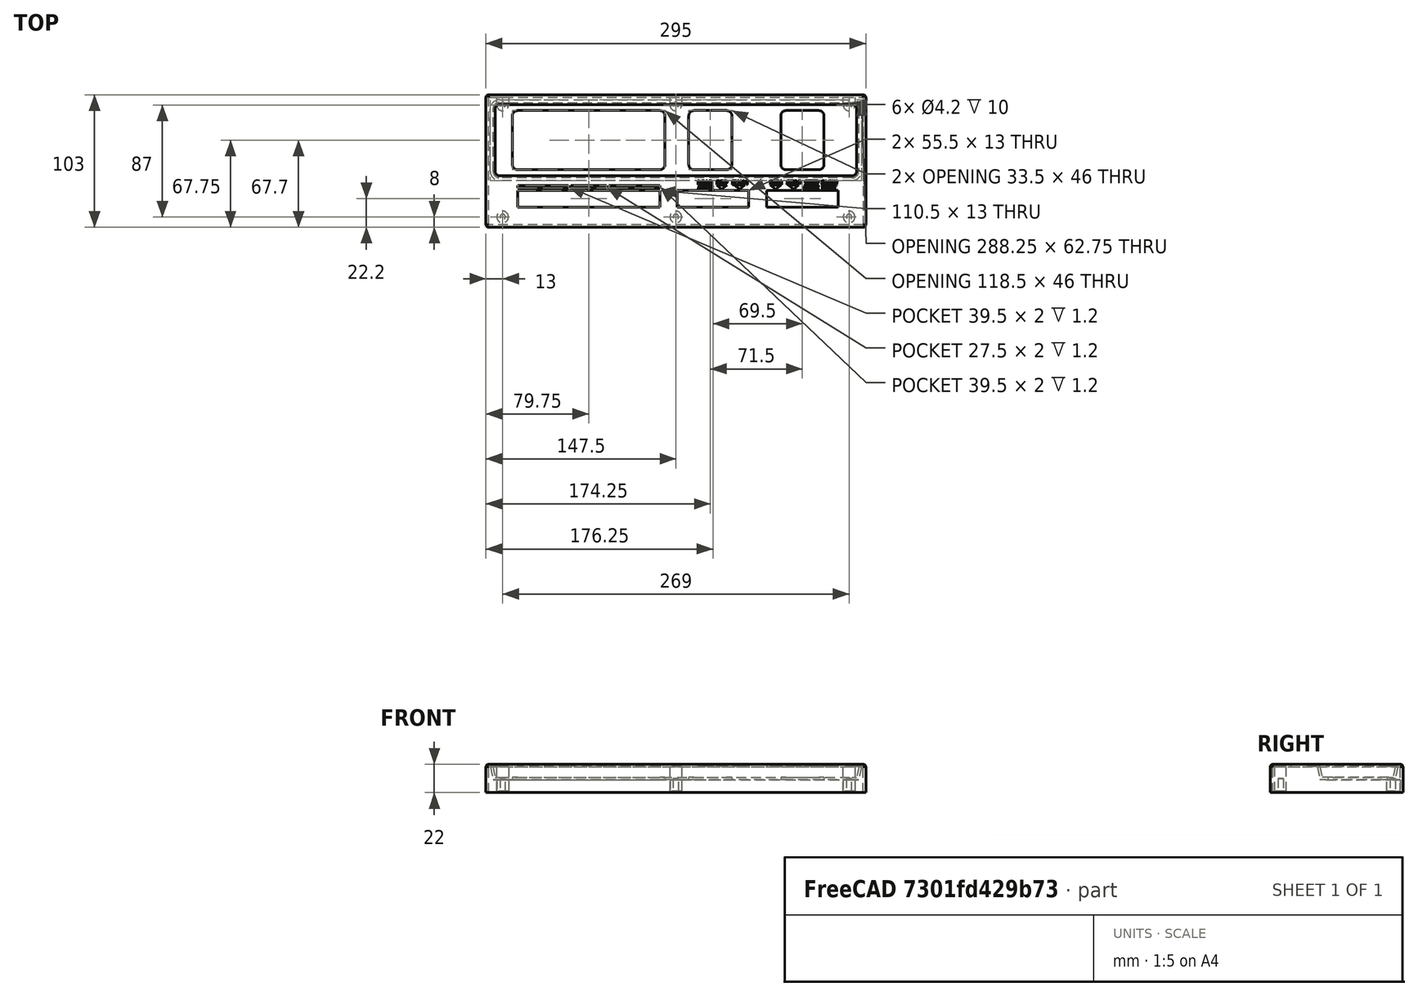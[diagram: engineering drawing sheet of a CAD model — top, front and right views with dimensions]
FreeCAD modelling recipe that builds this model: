
FCSTD DOCUMENT  (FreeCAD 0.21R33771 (Git))
Label: front panel
License: All rights reserved
LicenseURL: http://en.wikipedia.org/wiki/All_rights_reserved
objects: PartDesign::Pocket×14, Part::Part2DObjectPython×13, Sketcher::SketchObject×7, PartDesign::LinearPattern×4, PartDesign::Pad×3, TechDraw::DrawViewDimension×3, PartDesign::Draft×1, PartDesign::Thickness×1, PartDesign::MultiTransform×1, TechDraw::DrawSVGTemplate×1, PartDesign::Body×1, TechDraw::DrawProjGroupItem×1, TechDraw::DrawProjGroup×1, TechDraw::DrawPage×1
note: 69 computed .brp shape members not serialized (recipe doc carries the construction recipe); baked Part::Feature solids carry a one-line shape summary decoded from their .brp

FEATURE [Sketcher::SketchObject] Sketch
  FullyConstrained = true
  MapMode = 5
  Support = -> [XY_Plane]
  sketch-geometry (4):
    g0: LineSegment StartX=-145.5 StartY=49.5 StartZ=0 EndX=145.5 EndY=49.5 EndZ=0
    g1: LineSegment StartX=145.5 StartY=49.5 StartZ=0 EndX=145.5 EndY=-49.5 EndZ=0
    g2: LineSegment StartX=145.5 StartY=-49.5 StartZ=0 EndX=-145.5 EndY=-49.5 EndZ=0
    g3: LineSegment StartX=-145.5 StartY=-49.5 StartZ=0 EndX=-145.5 EndY=49.5 EndZ=0
  constraints (11):
    c: Coincident(g0,g1)
    c: Coincident(g1,g2)
    c: Coincident(g2,g3)
    c: Coincident(g3,g0)
    c: Horizontal(g0)
    c: Horizontal(g2)
    c: Vertical(g1)
    c: Vertical(g3)
    c: Symmetric(g1,g0,g-1)
    c: DistanceY(g3,g3) = 99
    c: DistanceX(g0,g0) = 291
FEATURE [PartDesign::Pad] Pad
  Direction = (0,0,1)
  Length = 20
  Length2 = 10
  Profile = -> Sketch
  ReferenceAxis = -> Sketch [N_Axis]
  Type = 0
FEATURE [Sketcher::SketchObject] Sketch001
  FullyConstrained = true
  MapMode = 5
  Placement = pos=(0,0,20) rot=(0,0,1;0rad)
  Support = -> [Pad]
  sketch-geometry (10):
    g0: ArcOfCircle CenterX=-137 CenterY=40.5 CenterZ=0 NormalX=0 NormalY=0 NormalZ=1 AngleXU=0 Radius=5 StartAngle=1.5708 EndAngle=3.14159
    g1: LineSegment StartX=-137 StartY=45.5 StartZ=0 EndX=137 EndY=45.5 EndZ=0
    g2: ArcOfCircle CenterX=137 CenterY=40.5 CenterZ=0 NormalX=0 NormalY=0 NormalZ=1 AngleXU=0 Radius=5 StartAngle=5e-16 EndAngle=1.5708
    g3: LineSegment StartX=142 StartY=40.5 StartZ=0 EndX=142 EndY=-8 EndZ=0
    g4: ArcOfCircle CenterX=137 CenterY=-8 CenterZ=0 NormalX=0 NormalY=0 NormalZ=1 AngleXU=0 Radius=5 StartAngle=4.71239 EndAngle=6.28319
    g5: LineSegment StartX=137 StartY=-13 StartZ=0 EndX=-137 EndY=-13 EndZ=0
    g6: ArcOfCircle CenterX=-137 CenterY=-8 CenterZ=0 NormalX=0 NormalY=0 NormalZ=1 AngleXU=0 Radius=5 StartAngle=3.14159 EndAngle=4.71239
    g7: LineSegment StartX=-142 StartY=-8 StartZ=0 EndX=-142 EndY=40.5 EndZ=0
    g8: GeomPoint X=-142 Y=45.5 Z=0
    g9: GeomPoint X=142 Y=-13 Z=0
  constraints (23):
    c: Tangent(g0,g1) = 1.5708
    c: Tangent(g1,g2) = 1.5708
    c: Tangent(g2,g3) = 1.5708
    c: Tangent(g3,g4) = 1.5708
    c: Tangent(g4,g5) = 1.5708
    c: Tangent(g5,g6) = 1.5708
    c: Tangent(g6,g7) = 1.5708
    c: Tangent(g7,g0) = 1.5708
    c: Horizontal(g1)
    c: Horizontal(g5)
    c: Vertical(g3)
    c: Vertical(g7)
    c: Equal(g2,g4)
    c: Equal(g4,g6)
    c: PointOnObject(g8,g1)
    c: PointOnObject(g8,g7)
    c: PointOnObject(g9,g3)
    c: PointOnObject(g9,g5)
    c: Diameter(g2) = 10
    c: DistanceX(g0,g2) = 284
    c: Symmetric(g0,g2,g-2)
    c: DistanceY(g-1,g0) = 45.5
    c: DistanceY(g5,g-1) = 13
FEATURE [PartDesign::Pocket] Pocket
  BaseFeature = -> Pad
  Direction = (0,0,-1)
  Length = 10
  Length2 = 5
  Profile = -> Sketch001
  ReferenceAxis = -> Sketch001 [N_Axis]
  Type = 0
FEATURE [PartDesign::Draft] Draft
  Angle = 12
  Base = -> Pocket [Face10]
  BaseFeature = -> Pocket
  NeutralPlane = -> Pocket [Face15]
  SupportTransform = false
FEATURE [PartDesign::Thickness] Thickness
  Base = -> Draft [Face4]
  BaseFeature = -> Draft
  Intersection = false
  Join = 0
  Mode = 0
  SupportTransform = false
  Value = 2
FEATURE [Sketcher::SketchObject] Sketch002
  FullyConstrained = true
  MapMode = 5
  Placement = pos=(0,0,22) rot=(0,0,1;0rad)
  Support = -> [Thickness]
  sketch-geometry (42):
    g0: LineSegment StartX=-123 StartY=-22.8 StartZ=0 EndX=-12.5 EndY=-22.8 EndZ=0
    g1: LineSegment StartX=-12.5 StartY=-22.8 StartZ=0 EndX=-12.5 EndY=-35.8 EndZ=0
    g2: LineSegment StartX=-12.5 StartY=-35.8 StartZ=0 EndX=-123 EndY=-35.8 EndZ=0
    g3: LineSegment StartX=-123 StartY=-35.8 StartZ=0 EndX=-123 EndY=-22.8 EndZ=0
    g4: LineSegment StartX=1 StartY=-22.8 StartZ=0 EndX=56.5 EndY=-22.8 EndZ=0
    g5: LineSegment StartX=56.5 StartY=-22.8 StartZ=0 EndX=56.5 EndY=-35.8 EndZ=0
    g6: LineSegment StartX=56.5 StartY=-35.8 StartZ=0 EndX=1 EndY=-35.8 EndZ=0
    g7: LineSegment StartX=1 StartY=-35.8 StartZ=0 EndX=1 EndY=-22.8 EndZ=0
    g8: LineSegment StartX=70.5 StartY=-22.8 StartZ=0 EndX=126 EndY=-22.8 EndZ=0
    g9: LineSegment StartX=126 StartY=-22.8 StartZ=0 EndX=126 EndY=-35.8 EndZ=0
    g10: LineSegment StartX=126 StartY=-35.8 StartZ=0 EndX=70.5 EndY=-35.8 EndZ=0
    g11: LineSegment StartX=70.5 StartY=-35.8 StartZ=0 EndX=70.5 EndY=-22.8 EndZ=0
    g12: ArcOfCircle CenterX=-123 CenterY=35.2 CenterZ=0 NormalX=0 NormalY=0 NormalZ=1 AngleXU=0 Radius=4 StartAngle=1.5708 EndAngle=3.14159
    g13: LineSegment StartX=-123 StartY=39.2 StartZ=0 EndX=-12.5 EndY=39.2 EndZ=0
    g14: ArcOfCircle CenterX=-12.5 CenterY=35.2 CenterZ=0 NormalX=0 NormalY=0 NormalZ=1 AngleXU=0 Radius=4 StartAngle=1e-15 EndAngle=1.5708
    g15: LineSegment StartX=-8.5 StartY=35.2 StartZ=0 EndX=-8.5 EndY=-2.8 EndZ=0
    g16: ArcOfCircle CenterX=-12.5 CenterY=-2.8 CenterZ=0 NormalX=0 NormalY=0 NormalZ=1 AngleXU=0 Radius=4 StartAngle=4.71239 EndAngle=6.28319
    g17: LineSegment StartX=-12.5 StartY=-6.8 StartZ=0 EndX=-123 EndY=-6.8 EndZ=0
    g18: ArcOfCircle CenterX=-123 CenterY=-2.8 CenterZ=0 NormalX=0 NormalY=0 NormalZ=1 AngleXU=0 Radius=4 StartAngle=3.14159 EndAngle=4.71239
    g19: LineSegment StartX=-127 StartY=-2.8 StartZ=0 EndX=-127 EndY=35.2 EndZ=0
    g20: GeomPoint X=-127 Y=39.2 Z=0
    g21: GeomPoint X=-8.5 Y=-6.8 Z=0
    g22: ArcOfCircle CenterX=14 CenterY=35.2 CenterZ=0 NormalX=0 NormalY=0 NormalZ=1 AngleXU=0 Radius=4 StartAngle=1.5708 EndAngle=3.14159
    g23: LineSegment StartX=14 StartY=39.2 StartZ=0 EndX=39.5 EndY=39.2 EndZ=0
    g24: ArcOfCircle CenterX=39.5 CenterY=35.2 CenterZ=0 NormalX=0 NormalY=0 NormalZ=1 AngleXU=0 Radius=4 StartAngle=-9e-16 EndAngle=1.5708
    g25: LineSegment StartX=43.5 StartY=35.2 StartZ=0 EndX=43.5 EndY=-2.8 EndZ=0
    g26: ArcOfCircle CenterX=39.5 CenterY=-2.8 CenterZ=0 NormalX=0 NormalY=0 NormalZ=1 AngleXU=0 Radius=4 StartAngle=4.71239 EndAngle=6.28319
    g27: LineSegment StartX=39.5 StartY=-6.8 StartZ=0 EndX=14 EndY=-6.8 EndZ=0
    g28: ArcOfCircle CenterX=14 CenterY=-2.8 CenterZ=0 NormalX=0 NormalY=0 NormalZ=1 AngleXU=0 Radius=4 StartAngle=3.14159 EndAngle=4.71239
    g29: LineSegment StartX=10 StartY=-2.8 StartZ=0 EndX=10 EndY=35.2 EndZ=0
    g30: GeomPoint X=10 Y=39.2 Z=0
    g31: GeomPoint X=43.5 Y=-6.8 Z=0
    g32: ArcOfCircle CenterX=85.5 CenterY=35.2 CenterZ=0 NormalX=0 NormalY=0 NormalZ=1 AngleXU=0 Radius=4 StartAngle=1.5708 EndAngle=3.14159
    g33: LineSegment StartX=85.5 StartY=39.2 StartZ=0 EndX=111 EndY=39.2 EndZ=0
    g34: ArcOfCircle CenterX=111 CenterY=35.2 CenterZ=0 NormalX=0 NormalY=0 NormalZ=1 AngleXU=0 Radius=4 StartAngle=-9e-16 EndAngle=1.5708
    g35: LineSegment StartX=115 StartY=35.2 StartZ=0 EndX=115 EndY=-2.8 EndZ=0
    g36: ArcOfCircle CenterX=111 CenterY=-2.8 CenterZ=0 NormalX=0 NormalY=0 NormalZ=1 AngleXU=0 Radius=4 StartAngle=4.71239 EndAngle=6.28319
    g37: LineSegment StartX=111 StartY=-6.8 StartZ=0 EndX=85.5 EndY=-6.8 EndZ=0
    g38: ArcOfCircle CenterX=85.5 CenterY=-2.8 CenterZ=0 NormalX=0 NormalY=0 NormalZ=1 AngleXU=0 Radius=4 StartAngle=3.14159 EndAngle=4.71239
    g39: LineSegment StartX=81.5 StartY=-2.8 StartZ=0 EndX=81.5 EndY=35.2 EndZ=0
    g40: GeomPoint X=81.5 Y=39.2 Z=0
    g41: GeomPoint X=115 Y=-6.8 Z=0
  constraints (108):
    c: Coincident(g0,g1)
    c: Coincident(g1,g2)
    c: Coincident(g2,g3)
    c: Coincident(g3,g0)
    c: Horizontal(g0)
    c: Horizontal(g2)
    c: Vertical(g1)
    c: Vertical(g3)
    c: Coincident(g4,g5)
    c: Coincident(g5,g6)
    c: Coincident(g6,g7)
    c: Coincident(g7,g4)
    c: Horizontal(g4)
    c: Horizontal(g6)
    c: Vertical(g5)
    c: Vertical(g7)
    c: Coincident(g8,g9)
    c: Coincident(g9,g10)
    c: Coincident(g10,g11)
    c: Coincident(g11,g8)
    c: Horizontal(g8)
    c: Horizontal(g10)
    c: Vertical(g9)
    c: Vertical(g11)
    c: Horizontal(g10,g5)
    c: Horizontal(g5,g1)
    c: Horizontal(g4,g0)
    c: Horizontal(g0,g8)
    c: DistanceY(g3,g3) = 13
    c: DistanceX(g2,g-1) = 123
    c: DistanceX(g0,g0) = 110.5
    c: DistanceY(g1,g-1) = 35.8
    c: DistanceX(g0,g4) = 13.5
    c: DistanceX(g4,g4) = 55.5
    c: DistanceX(g4,g8) = 14
    c: Equal(g8,g4)
    c: Tangent(g12,g13) = 1.5708
    c: Tangent(g13,g14) = 1.5708
    c: Tangent(g14,g15) = 1.5708
    c: Tangent(g15,g16) = 1.5708
    c: Tangent(g16,g17) = 1.5708
    c: Tangent(g17,g18) = 1.5708
    c: Tangent(g18,g19) = 1.5708
    c: Tangent(g19,g12) = 1.5708
    c: Horizontal(g13)
    c: Horizontal(g17)
    c: Vertical(g15)
    c: Vertical(g19)
    c: Equal(g12,g14)
    c: Equal(g14,g16)
    c: Equal(g16,g18)
    c: PointOnObject(g20,g13)
    c: PointOnObject(g20,g19)
    c: PointOnObject(g21,g15)
    c: PointOnObject(g21,g17)
    c: Radius(g12) = 4
    c: Vertical(g17,g0)
    c: Vertical(g16,g0)
    c: Tangent(g22,g23) = 1.5708
    c: Tangent(g23,g24) = 1.5708
    c: Tangent(g24,g25) = 1.5708
    c: Tangent(g25,g26) = 1.5708
    c: Tangent(g26,g27) = 1.5708
    c: Tangent(g27,g28) = 1.5708
    c: Tangent(g28,g29) = 1.5708
    c: Tangent(g29,g22) = 1.5708
    c: Horizontal(g23)
    c: Horizontal(g27)
    c: Vertical(g25)
    c: Vertical(g29)
    c: Equal(g22,g24)
    c: Equal(g24,g26)
    c: Equal(g26,g28)
    c: PointOnObject(g30,g23)
    c: PointOnObject(g30,g29)
    c: PointOnObject(g31,g25)
    c: PointOnObject(g31,g27)
    c: Equal(g26,g14)
    c: Horizontal(g22,g13)
    c: Horizontal(g27,g16)
    c: DistanceX(g26,g4) = 17
    c: DistanceX(g4,g27) = 13
    c: Tangent(g32,g33) = 1.5708
    c: Tangent(g33,g34) = 1.5708
    c: Tangent(g34,g35) = 1.5708
    c: Tangent(g35,g36) = 1.5708
    c: Tangent(g36,g37) = 1.5708
    c: Tangent(g37,g38) = 1.5708
    c: Tangent(g38,g39) = 1.5708
    c: Tangent(g39,g32) = 1.5708
    c: Horizontal(g33)
    c: Horizontal(g37)
    c: Vertical(g35)
    c: Vertical(g39)
    c: Equal(g32,g34)
    c: Equal(g34,g36)
    c: Equal(g36,g38)
    c: PointOnObject(g40,g33)
    c: PointOnObject(g40,g39)
    c: PointOnObject(g41,g35)
    c: PointOnObject(g41,g37)
    c: Horizontal(g23,g32)
    c: Equal(g32,g24)
    c: DistanceX(g36,g8) = 15
    c: DistanceY(g8,g35) = 20
    c: DistanceY(g8,g33) = 62
    c: Horizontal(g37,g16)
    c: Equal(g37,g27)
FEATURE [PartDesign::Pocket] Pocket001  label="Switch cut out"
  BaseFeature = -> Thickness
  Direction = (0,0,-1)
  Length = 5
  Length2 = 5
  Profile = -> Sketch002
  ReferenceAxis = -> Sketch002 [N_Axis]
  Type = 1
FEATURE [Sketcher::SketchObject] Sketch003
  FullyConstrained = true
  MapMode = 5
  Placement = pos=(0,0,20) rot=(1,0,0;3.14159rad)
  Support = -> [Pocket001]
  sketch-geometry (1):
    g0: Circle CenterX=-134.5 CenterY=43.5 CenterZ=0 NormalX=0 NormalY=0 NormalZ=1 AngleXU=0 Radius=4.5
  constraints (3):
    c: DistanceY(g-1,g0) = 43.5
    c: DistanceX(g0,g-1) = 134.5
    c: Diameter(g0) = 9
FEATURE [PartDesign::Pad] Pad001
  BaseFeature = -> Pocket001
  Direction = (0,0,-1)
  Length = 19
  Length2 = 10
  Profile = -> Sketch003
  ReferenceAxis = -> Sketch003 [N_Axis]
  Type = 0
FEATURE [PartDesign::LinearPattern] LinearPattern
  BaseFeature = -> Pad001
  Direction = -> Sketch003 [H_Axis]
  Length = 269
  Occurrences = 3
  Originals = -> [Pad001]
FEATURE [Sketcher::SketchObject] Sketch004
  ExternalGeometry = -> [LinearPattern]
  FullyConstrained = true
  MapMode = 5
  Placement = pos=(0,0,10) rot=(1,0,0;3.14159rad)
  Support = -> [LinearPattern]
  sketch-geometry (4):
    g0: ArcOfCircle CenterX=-134.5 CenterY=-43.5 CenterZ=0 NormalX=0 NormalY=0 NormalZ=1 AngleXU=0 Radius=4.5 StartAngle=-9e-16 EndAngle=3.14159
    g1: LineSegment StartX=-139 StartY=-43.5 StartZ=0 EndX=-139 EndY=-49.5 EndZ=0
    g2: LineSegment StartX=-139 StartY=-49.5 StartZ=0 EndX=-130 EndY=-49.5 EndZ=0
    g3: LineSegment StartX=-130 StartY=-49.5 StartZ=0 EndX=-130 EndY=-43.5 EndZ=0
  constraints (11):
    c: Tangent(g0,g1) = -1.5708
    c: Coincident(g1,g2)
    c: PointOnObject(g2,g-3)
    c: Horizontal(g2)
    c: Coincident(g2,g3)
    c: Vertical(g3)
    c: Vertical(g1)
    c: Diameter(g0) = 9
    c: DistanceX(g0,g-1) = 134.5
    c: DistanceY(g0,g-1) = 43.5
    c: Tangent(g3,g0) = -1.5708
FEATURE [PartDesign::Pad] Pad002
  BaseFeature = -> LinearPattern
  Direction = (0,0,-1)
  Length = 9
  Length2 = 10
  Profile = -> Sketch004
  ReferenceAxis = -> Sketch004 [N_Axis]
  Type = 0
FEATURE [PartDesign::LinearPattern] LinearPattern001
  BaseFeature = -> Pad002
  Direction = -> Sketch004 [H_Axis]
  Length = 269
  Occurrences = 3
  Originals = -> [Pad002]
FEATURE [Sketcher::SketchObject] Sketch005
  ExternalGeometry = -> [LinearPattern001]
  FullyConstrained = true
  MapMode = 5
  Placement = pos=(0,0,1) rot=(1,0,0;3.14159rad)
  Support = -> [LinearPattern001]
  sketch-geometry (1):
    g0: Circle CenterX=-134.5 CenterY=43.5 CenterZ=0 NormalX=0 NormalY=0 NormalZ=1 AngleXU=0 Radius=2.1
  constraints (2):
    c: Coincident(g0,g-3)
    c: Diameter(g0) = 4.2
FEATURE [PartDesign::Pocket] Pocket002
  BaseFeature = -> LinearPattern001
  Direction = (0,0,1)
  Length = 10
  Length2 = 5
  Profile = -> Sketch005
  ReferenceAxis = -> Sketch005 [N_Axis]
  Type = 0
FEATURE [PartDesign::LinearPattern] LinearPattern002
  Direction = -> Sketch005 [H_Axis]
  Length = 269
  Occurrences = 3
FEATURE [PartDesign::LinearPattern] LinearPattern003
  Direction = -> Sketch005 [V_Axis]
  Length = 87
  Occurrences = 2
  Reversed = true
FEATURE [PartDesign::MultiTransform] MultiTransform
  BaseFeature = -> Pocket002
  Originals = -> [Pocket002]
  Transformations = -> [LinearPattern002,LinearPattern003]
FEATURE [TechDraw::DrawSVGTemplate] Template
  EditableTexts = APPROVER_NAME=APPROVER NAME; AUTHOR_NAME=AUTHOR NAME; DATE=YYYY-MM-DD; DN=DN; DOCUMENT_TYPE=Mechanical assembly drawing; OWNER_NAME=OWNER NAME; PM=PM; PN=PN; REVISION=REV A; RIGHTS=(R) DO NOT DUPLICATE THIS DRAWING TO THIRD PARTIES WITHOUT OWNER'S PERMISSION!; SCALE=M x:x; SHEET=99 of 99; SIZE=A3; TITLELINE-1=FreeCAD; TOLERANCE=+/- ?
  Height = 297
  Orientation = 1
  Template = /Applications/FreeCAD.app/Contents/Resources/share/Mod/TechDraw/Templates/A3_Landscape_ISO7200_Pep.svg
  Width = 420
FEATURE [Sketcher::SketchObject] Sketch006
  ExternalGeometry = -> [MultiTransform]
  FullyConstrained = true
  MapMode = 5
  Placement = pos=(0,0,22) rot=(0,0,1;0rad)
  Support = -> [MultiTransform]
  sketch-geometry (28):
    g0: LineSegment StartX=-123 StartY=-19.098 StartZ=0 EndX=-83.5 EndY=-19.098 EndZ=0
    g1: LineSegment StartX=-83.5 StartY=-19.098 StartZ=0 EndX=-83.5 EndY=-21.098 EndZ=0
    g2: LineSegment StartX=-83.5 StartY=-21.098 StartZ=0 EndX=-123 EndY=-21.098 EndZ=0
    g3: LineSegment StartX=-123 StartY=-21.098 StartZ=0 EndX=-123 EndY=-19.098 EndZ=0
    g4: LineSegment StartX=-81.5 StartY=-19.098 StartZ=0 EndX=-54 EndY=-19.098 EndZ=0
    g5: LineSegment StartX=-54 StartY=-19.098 StartZ=0 EndX=-54 EndY=-21.098 EndZ=0
    g6: LineSegment StartX=-54 StartY=-21.098 StartZ=0 EndX=-81.5 EndY=-21.098 EndZ=0
    g7: LineSegment StartX=-81.5 StartY=-21.098 StartZ=0 EndX=-81.5 EndY=-19.098 EndZ=0
    g8: LineSegment StartX=-52 StartY=-19.098 StartZ=0 EndX=-12.5 EndY=-19.098 EndZ=0
    g9: LineSegment StartX=-12.5 StartY=-19.098 StartZ=0 EndX=-12.5 EndY=-21.098 EndZ=0
    g10: LineSegment StartX=-12.5 StartY=-21.098 StartZ=0 EndX=-52 EndY=-21.098 EndZ=0
    g11: LineSegment StartX=-52 StartY=-21.098 StartZ=0 EndX=-52 EndY=-19.098 EndZ=0
    g12: LineSegment StartX=53.5 StartY=-18.8 StartZ=0 EndX=45.5 EndY=-18.8 EndZ=0
    g13: LineSegment StartX=45.5 StartY=-18.8 StartZ=0 EndX=49.5 EndY=-21.8 EndZ=0
    g14: LineSegment StartX=49.5 StartY=-21.8 StartZ=0 EndX=53.5 EndY=-18.8 EndZ=0
    g15: Circle CenterX=49.5 CenterY=-17.6333 CenterZ=0 NormalX=0 NormalY=0 NormalZ=1 AngleXU=0 Radius=4.16667
    g16: LineSegment StartX=35.7 StartY=-21.8 StartZ=0 EndX=39.7 EndY=-18.8 EndZ=0
    g17: LineSegment StartX=39.7 StartY=-18.8 StartZ=0 EndX=31.7 EndY=-18.8 EndZ=0
    g18: LineSegment StartX=31.7 StartY=-18.8 StartZ=0 EndX=35.7 EndY=-21.8 EndZ=0
    g19: Circle CenterX=35.7 CenterY=-17.6333 CenterZ=0 NormalX=0 NormalY=0 NormalZ=1 AngleXU=0 Radius=4.16667
    g20: LineSegment StartX=77.5 StartY=-21.8 StartZ=0 EndX=81.5 EndY=-18.8 EndZ=0
    g21: LineSegment StartX=81.5 StartY=-18.8 StartZ=0 EndX=73.5 EndY=-18.8 EndZ=0
    g22: LineSegment StartX=73.5 StartY=-18.8 StartZ=0 EndX=77.5 EndY=-21.8 EndZ=0
    g23: Circle CenterX=77.5 CenterY=-17.6333 CenterZ=0 NormalX=0 NormalY=0 NormalZ=1 AngleXU=0 Radius=4.16667
    g24: LineSegment StartX=91.3 StartY=-21.8 StartZ=0 EndX=95.3 EndY=-18.8 EndZ=0
    g25: LineSegment StartX=95.3 StartY=-18.8 StartZ=0 EndX=87.3 EndY=-18.8 EndZ=0
    g26: LineSegment StartX=87.3 StartY=-18.8 StartZ=0 EndX=91.3 EndY=-21.8 EndZ=0
    g27: Circle CenterX=91.3 CenterY=-17.6333 CenterZ=0 NormalX=0 NormalY=0 NormalZ=1 AngleXU=0 Radius=4.16667
  constraints (84):
    c: Coincident(g0,g1)
    c: Coincident(g1,g2)
    c: Coincident(g2,g3)
    c: Coincident(g3,g0)
    c: Horizontal(g0)
    c: Horizontal(g2)
    c: Vertical(g1)
    c: Vertical(g3)
    c: Coincident(g4,g5)
    c: Coincident(g5,g6)
    c: Coincident(g6,g7)
    c: Coincident(g7,g4)
    c: Horizontal(g4)
    c: Horizontal(g6)
    c: Vertical(g5)
    c: Vertical(g7)
    c: Coincident(g8,g9)
    c: Coincident(g9,g10)
    c: Coincident(g10,g11)
    c: Coincident(g11,g8)
    c: Horizontal(g8)
    c: Horizontal(g10)
    c: Vertical(g9)
    c: Vertical(g11)
    c: DistanceY(g3,g3) = 2
    c: Vertical(g2,g-3)
    c: Equal(g8,g0)
    c: Horizontal(g6,g1)
    c: Horizontal(g1,g10)
    c: Horizontal(g8,g4)
    c: Horizontal(g4,g0)
    c: Vertical(g9,g-4)
    c: DistanceY(g-3,g2) = 1.702
    c: DistanceX(g0,g4) = 2
    c: DistanceX(g4,g8) = 2
    c: DistanceX(g8,g8) = 39.5
    c: Coincident(g12,g13)
    c: Coincident(g13,g14)
    c: Coincident(g14,g12)
    c: PointOnObject(g12,g15)
    c: PointOnObject(g13,g15)
    c: PointOnObject(g14,g15)
    c: Coincident(g16,g17)
    c: Coincident(g17,g18)
    c: Coincident(g18,g16)
    c: Equal(g16,g18)
    c: PointOnObject(g16,g19)
    c: PointOnObject(g17,g19)
    c: PointOnObject(g18,g19)
    c: Horizontal(g17)
    c: Horizontal(g12)
    c: Equal(g16,g13)
    c: DistanceX(g19,g15) = 13.8
    c: Equal(g17,g12)
    c: Horizontal(g16,g12)
    c: Equal(g14,g13)
    c: DistanceX(g17,g17) = 8
    c: DistanceY(g16,g16) = 3
    c: DistanceX(g13,g-5) = 7
    c: DistanceY(g-5,g13) = 1
    c: Coincident(g20,g21)
    c: Coincident(g21,g22)
    c: Coincident(g22,g20)
    c: Equal(g20,g22)
    c: PointOnObject(g20,g23)
    c: PointOnObject(g21,g23)
    c: PointOnObject(g22,g23)
    c: Coincident(g24,g25)
    c: Coincident(g25,g26)
    c: Coincident(g26,g24)
    c: Equal(g24,g26)
    c: PointOnObject(g24,g27)
    c: PointOnObject(g25,g27)
    c: PointOnObject(g26,g27)
    c: Horizontal(g25,g20)
    c: Horizontal(g25)
    c: Horizontal(g21)
    c: DistanceX(g23,g27) = 13.8
    c: Equal(g21,g25)
    c: Equal(g25,g12)
    c: DistanceY(g20,g20) = 3
    c: Horizontal(g24,g20)
    c: Horizontal(g12,g21)
    c: DistanceX(g-6,g20) = 7
FEATURE [PartDesign::Pocket] Pocket003  label="Down arrows"
  BaseFeature = -> MultiTransform
  Direction = (0,0,-1)
  Length = 1.2
  Length2 = 5
  Profile = -> Sketch006
  ReferenceAxis = -> Sketch006 [N_Axis]
  Type = 0
FEATURE [Part::Part2DObjectPython] ShapeString  label="DEP"  # Draft 2D object (typed FeaturePython)
  FontFile = <userpath>/Downloads/roboto/Roboto-Black.ttf
  MakeFace = true
  Placement = pos=(31.5,-18.5,22) rot=(0,0,1;0rad)
  Size = 4
  String = DEP
  Tracking = 0
FEATURE [Part::Part2DObjectPython] ShapeString001  label="LOAD"  # Draft 2D object (typed FeaturePython)
  FontFile = <userpath>/Downloads/roboto/Roboto-Black.ttf
  MakeFace = true
  Placement = pos=(17,-18.5,22) rot=(0,0,1;0rad)
  Size = 4
  String = LOAD
  Tracking = 0
FEATURE [Part::Part2DObjectPython] ShapeString002  label="ADDR"  # Draft 2D object (typed FeaturePython)
  FontFile = <userpath>/Downloads/roboto/Roboto-Black.ttf
  MakeFace = true
  Placement = pos=(17,-22.25,22) rot=(0.987988,-0.125405,-0.090301;0rad)
  Size = 4
  String = ADDR
  Tracking = 0
FEATURE [PartDesign::Pocket] Pocket004  label="DEP Pocket"
  BaseFeature = -> Pocket003
  Direction = (0,0,-1)
  Length = 1.2
  Length2 = 5
  Profile = -> ShapeString
  ReferenceAxis = -> ShapeString [N_Axis]
  Type = 0
FEATURE [PartDesign::Pocket] Pocket005  label="Load Pocket"
  BaseFeature = -> Pocket004
  Direction = (0,0,-1)
  Length = 1.2
  Length2 = 5
  Profile = -> ShapeString001
  ReferenceAxis = -> ShapeString001 [N_Axis]
  Type = 0
FEATURE [PartDesign::Pocket] Pocket006  label="ADDR Pocket"
  BaseFeature = -> Pocket005
  Direction = (0,0,-1)
  Length = 1.2
  Length2 = 5
  Profile = -> ShapeString002
  ReferenceAxis = -> ShapeString002 [N_Axis]
  Type = 0
FEATURE [Part::Part2DObjectPython] ShapeString003  label="EXAM"  # Draft 2D object (typed FeaturePython)
  FontFile = <userpath>/Downloads/roboto/Roboto-Black.ttf
  MakeFace = true
  Placement = pos=(43.5,-18.5,22) rot=(0,0,1;0rad)
  Size = 4
  String = EXAM
  Tracking = 0
FEATURE [PartDesign::Pocket] Pocket007
  BaseFeature = -> Pocket006
  Direction = (0,0,-1)
  Length = 1
  Length2 = 5
  Profile = -> ShapeString003
  ReferenceAxis = -> ShapeString003 [N_Axis]
  Type = 0
FEATURE [Part::Part2DObjectPython] ShapeString004  # Draft 2D object (typed FeaturePython)
  FontFile = <userpath>/Downloads/roboto/Roboto-Black.ttf
  MakeFace = true
  Placement = pos=(73,-18.5,22) rot=(0,0,1;0rad)
  Size = 4
  String = RUN
  Tracking = 0
FEATURE [Part::Part2DObjectPython] ShapeString005  # Draft 2D object (typed FeaturePython)
  FontFile = <userpath>/Downloads/roboto/Roboto-Black.ttf
  MakeFace = true
  Placement = pos=(86,-18.5,22) rot=(0,0,1;0rad)
  Size = 4
  String = STOP
  Tracking = 0
FEATURE [Part::Part2DObjectPython] ShapeString006  # Draft 2D object (typed FeaturePython)
  FontFile = <userpath>/Downloads/roboto/Roboto-Black.ttf
  MakeFace = true
  Placement = pos=(100,-18.5,22) rot=(0,0,1;0rad)
  Size = 4
  String = STEP
  Tracking = 0
FEATURE [Part::Part2DObjectPython] ShapeString007  # Draft 2D object (typed FeaturePython)
  FontFile = <userpath>/Downloads/roboto/Roboto-Black.ttf
  MakeFace = true
  Placement = pos=(113,-18.5,22) rot=(0,0,1;0rad)
  Size = 4
  String = SLOW
  Tracking = 0
FEATURE [Part::Part2DObjectPython] ShapeString008  # Draft 2D object (typed FeaturePython)
  FontFile = <userpath>/Downloads/roboto/Roboto-Black.ttf
  MakeFace = true
  Placement = pos=(99.5,-22.25,22) rot=(0,0,1;0rad)
  Size = 4
  String = CONT
  Tracking = 0
FEATURE [Part::Part2DObjectPython] ShapeString009  label="FAST"  # Draft 2D object (typed FeaturePython)
  FontFile = <userpath>/Downloads/roboto/Roboto-Black.ttf
  MakeFace = true
  Placement = pos=(113.5,-22.25,22) rot=(0,0,1;0rad)
  Size = 4
  String = FAST
  Tracking = 0
FEATURE [PartDesign::Pocket] Pocket008  label="RUN"
  BaseFeature = -> Pocket007
  Direction = (0,0,-1)
  Length = 1.5
  Length2 = 5
  Profile = -> ShapeString004
  ReferenceAxis = -> ShapeString004 [N_Axis]
  Type = 0
FEATURE [PartDesign::Pocket] Pocket009  label="STOP"
  BaseFeature = -> Pocket008
  Direction = (0,0,-1)
  Length = 1.2
  Length2 = 5
  Profile = -> ShapeString005
  ReferenceAxis = -> ShapeString005 [N_Axis]
  Type = 0
FEATURE [PartDesign::Pocket] Pocket010  label="STEP"
  BaseFeature = -> Pocket009
  Direction = (0,0,-1)
  Length = 1.2
  Length2 = 5
  Profile = -> ShapeString006
  ReferenceAxis = -> ShapeString006 [N_Axis]
  Type = 0
FEATURE [PartDesign::Pocket] Pocket011  label="SLOW"
  BaseFeature = -> Pocket010
  Direction = (0,0,-1)
  Length = 1.2
  Length2 = 5
  Profile = -> ShapeString007
  ReferenceAxis = -> ShapeString007 [N_Axis]
  Type = 0
FEATURE [PartDesign::Pocket] Pocket012  label="CONT"
  BaseFeature = -> Pocket011
  Direction = (0,0,-1)
  Length = 1.2
  Length2 = 5
  Profile = -> ShapeString008
  ReferenceAxis = -> ShapeString008 [N_Axis]
  Type = 0
FEATURE [PartDesign::Pocket] Pocket013  label="FAST001"
  BaseFeature = -> Pocket012
  Direction = (0,0,-1)
  Length = 1.2
  Length2 = 5
  Profile = -> ShapeString009
  ReferenceAxis = -> ShapeString009 [N_Axis]
  Type = 0
FEATURE [PartDesign::Body] Body
  Group = -> [Sketch,Pad,Sketch001,Pocket,Draft,Thickness,Sketch002,Pocket001,Sketch003,Pad001,LinearPattern,Sketch004,Pad002,LinearPattern001,Sketch005,Pocket002,MultiTransform,LinearPattern002,LinearPattern003,Sketch006,Pocket003,ShapeString,ShapeString001,ShapeString002,Pocket004,Pocket005,Pocket006,ShapeString003,Pocket007,ShapeString004,ShapeString005,ShapeString006,ShapeString007,ShapeString008,+7 more]
  Origin = -> Origin
  Tip = -> Pocket013
FEATURE [TechDraw::DrawProjGroupItem] ProjItem  label="Front"
  CoarseView = false
  Direction = (0,0,1)
  Focus = 100
  HardHidden = false
  IsoCount = 0
  IsoHidden = false
  IsoVisible = false
  LockPosition = true
  Perspective = false
  Rotation = 0
  RotationVector = (1,0,0)
  ScaleType = 2
  ScrubCount = 0
  SeamHidden = false
  SeamVisible = true
  SmoothHidden = false
  SmoothVisible = true
  Source = -> [Body]
  Type = 0
  X = 0
  XDirection = (1,0,0)
  Y = 0
FEATURE [TechDraw::DrawProjGroup] ProjGroup
  Anchor = -> ProjItem
  AutoDistribute = true
  LockPosition = false
  ProjectionType = 0
  Rotation = 0
  ScaleType = 0
  Source = -> [Body]
  Views = -> [ProjItem]
  X = 210
  Y = 148.5
  spacingX = 15
  spacingY = 15
FEATURE [TechDraw::DrawViewDimension] Dimension001
  AngleOverride = false
  Arbitrary = false
  ArbitraryTolerances = false
  EqualTolerance = true
  ExtensionAngle = 0
  FormatSpec = %.3f
  FormatSpecOverTolerance = %+.3f
  FormatSpecUnderTolerance = %+.3f
  Inverted = false
  LineAngle = 0
  LockPosition = false
  MeasureType = 1
  OverTolerance = 0
  References2D = -> [ProjItem]
  Rotation = 0
  ScaleType = 0
  TheoreticalExact = false
  Type = 2
  UnderTolerance = 0
  X = 168.608
  Y = 20.4136
FEATURE [TechDraw::DrawViewDimension] Dimension002
  AngleOverride = false
  Arbitrary = false
  ArbitraryTolerances = false
  EqualTolerance = true
  ExtensionAngle = 0
  FormatSpec = R%.3f
  FormatSpecOverTolerance = %+.3f
  FormatSpecUnderTolerance = %+.3f
  Inverted = false
  LineAngle = 0
  LockPosition = false
  MeasureType = 1
  OverTolerance = 0
  References2D = -> [ProjItem]
  Rotation = 0
  ScaleType = 0
  TheoreticalExact = false
  Type = 4
  UnderTolerance = 0
  X = -162.459
  Y = 43.8237
FEATURE [TechDraw::DrawViewDimension] Dimension
  AngleOverride = false
  Arbitrary = false
  ArbitraryTolerances = false
  EqualTolerance = true
  ExtensionAngle = 0
  FormatSpec = %.3f
  FormatSpecOverTolerance = %+.3f
  FormatSpecUnderTolerance = %+.3f
  Inverted = false
  LineAngle = 0
  LockPosition = false
  MeasureType = 1
  OverTolerance = 0
  References2D = -> [ProjItem]
  Rotation = 0
  ScaleType = 0
  TheoreticalExact = false
  Type = 1
  UnderTolerance = 0
  X = -6.9642
  Y = 88.1732
FEATURE [TechDraw::DrawPage] Page
  KeepUpdated = true
  NextBalloonIndex = 1
  ProjectionType = 0
  Template = -> Template
  Views = -> [ProjGroup,Dimension001,Dimension002,Dimension]
FEATURE [Part::Part2DObjectPython] ShapeString010  # Draft 2D object (typed FeaturePython)
  FontFile = <userpath>/Downloads/roboto/Roboto-Black.ttf
  MakeFace = true
  Placement = pos=(1.5,-18.5,22) rot=(0,0,1;0rad)
  Size = 4
  String = PAGE
  Tracking = 0
FEATURE [Part::Part2DObjectPython] ShapeString011  # Draft 2D object (typed FeaturePython)
  FontFile = <userpath>/Downloads/roboto/Roboto-Black.ttf
  MakeFace = true
  Placement = pos=(1,-22.25,22) rot=(0,0,1;0rad)
  Size = 4
  String = NORM
  Tracking = 0
FEATURE [Part::Part2DObjectPython] ShapeString012  # Draft 2D object (typed FeaturePython)
  FontFile = <userpath>/Downloads/roboto/Roboto-Black.ttf
  MakeFace = true
  Placement = pos=(2.5,-40,22) rot=(0,0,1;0rad)
  Size = 4
  String = ZER0
  Tracking = 0
